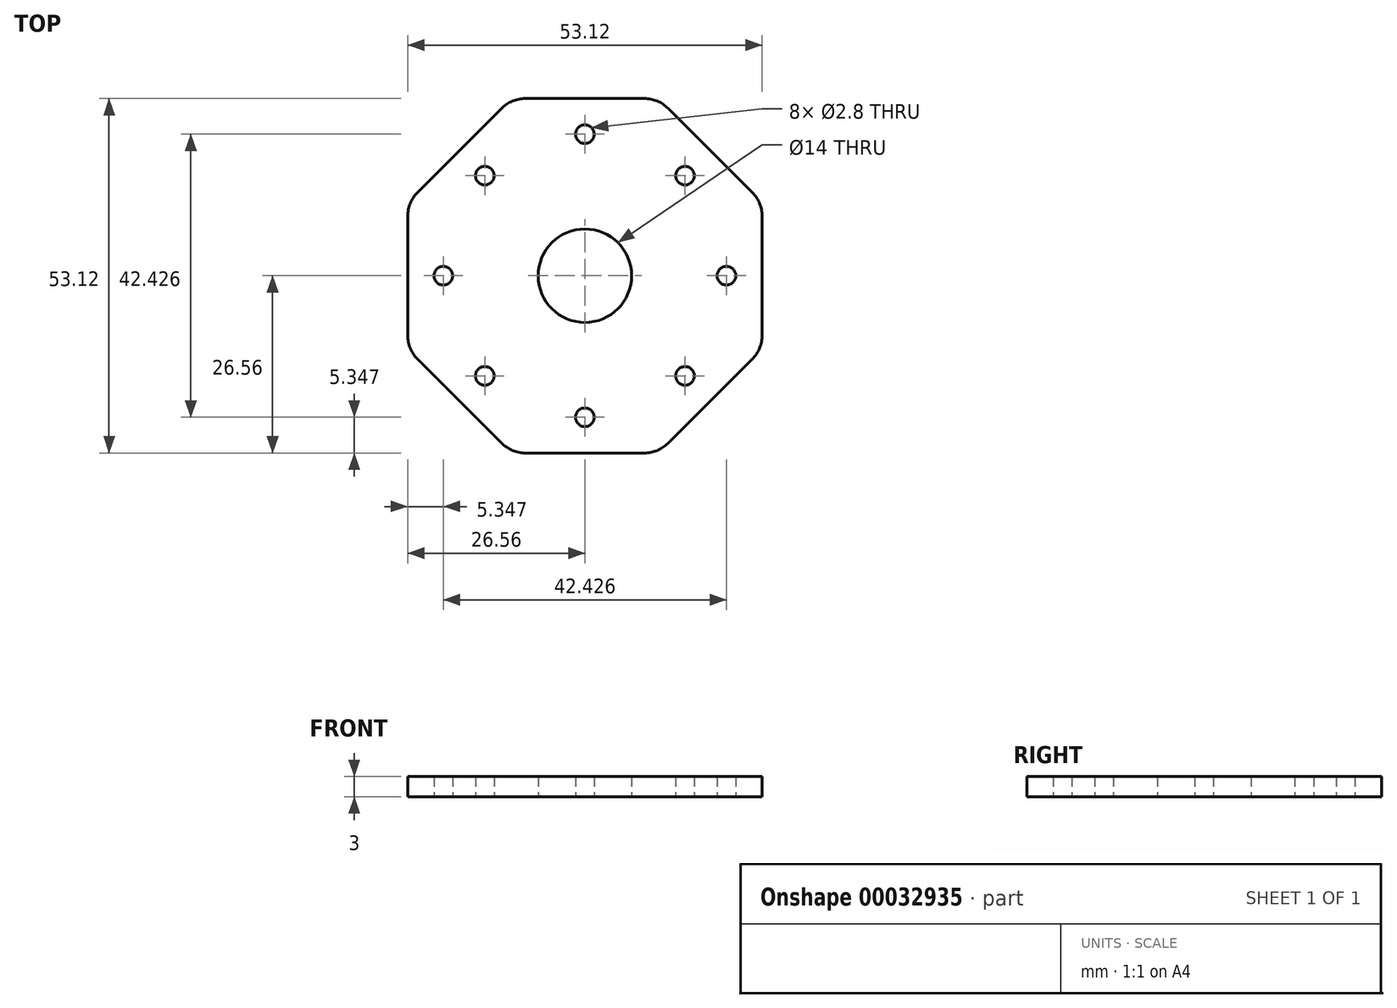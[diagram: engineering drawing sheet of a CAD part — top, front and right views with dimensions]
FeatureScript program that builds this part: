
annotation { "Feature Type Name" : "Feature", "Feature Type Description" : "" }
export const myFeature = defineFeature(function(context is Context, id is Id, definition is map)
    precondition{}
    {
        {
            var Q0;
            Q0=qCreatedBy(makeId("Top.planeOp"),FACE);
            var sketch = newSketch(context, id + "F0", { "sketchPlane" : qUnion([Q0])});
            skLineSegment(sketch, "E0.rect.bottom", {"start": v(15, -15) * mm, "end": v(-15, -15) * mm, "construction": true});
            skLineSegment(sketch, "E0.rect.top", {"start": v(15, 15) * mm, "end": v(-15, 15) * mm, "construction": true});
            skLineSegment(sketch, "E0.rect.left", {"start": v(15, -15) * mm, "end": v(15, 15) * mm, "construction": true});
            skLineSegment(sketch, "E0.rect.right", {"start": v(-15, -15) * mm, "end": v(-15, 15) * mm, "construction": true});
            skPoint(sketch, "E0.rect.middle", {"position": v(0, 0) * mm});
            skCircle(sketch, "E1.cCircle", {"center": v(0, 0) * mm, "radius": 21.21 * mm, "construction": true});
            skLineSegment(sketch, "E1.0", {"start": v(21.21, 0) * mm, "end": v(0, -21.21) * mm, "construction": true});
            skLineSegment(sketch, "E1.1", {"start": v(0, -21.21) * mm, "end": v(-21.21, 0) * mm, "construction": true});
            skLineSegment(sketch, "E1.2", {"start": v(-21.21, 0) * mm, "end": v(0, 21.21) * mm, "construction": true});
            skLineSegment(sketch, "E1.3", {"start": v(0, 21.21) * mm, "end": v(21.21, 0) * mm, "construction": true});
            skCircle(sketch, "E2", {"center": v(0, 21.21) * mm, "radius": 1.4 * mm});
            skCircle(sketch, "E3.1.0", {"center": v(-15, 15) * mm, "radius": 1.4 * mm});
            skCircle(sketch, "E3.2.0", {"center": v(-21.21, 0) * mm, "radius": 1.4 * mm});
            skCircle(sketch, "E3.3.0", {"center": v(-15, -15) * mm, "radius": 1.4 * mm});
            skCircle(sketch, "E3.4.0", {"center": v(0, -21.21) * mm, "radius": 1.4 * mm});
            skCircle(sketch, "E3.5.0", {"center": v(15, -15) * mm, "radius": 1.4 * mm});
            skCircle(sketch, "E3.6.0", {"center": v(21.21, 0) * mm, "radius": 1.4 * mm});
            skCircle(sketch, "E3.7.0", {"center": v(15, 15) * mm, "radius": 1.4 * mm});
            skCircle(sketch, "E4.cCircle", {"center": v(0, 0) * mm, "radius": 26.56 * mm, "construction": true});
            skLineSegment(sketch, "E4.0", {"start": v(-8.93, 26.56) * mm, "end": v(8.93, 26.56) * mm});
            skLineSegment(sketch, "E4.1", {"start": v(12.46, 25.1) * mm, "end": v(25.1, 12.46) * mm});
            skLineSegment(sketch, "E4.2", {"start": v(26.56, 8.93) * mm, "end": v(26.56, -8.93) * mm});
            skLineSegment(sketch, "E4.3", {"start": v(25.1, -12.46) * mm, "end": v(12.46, -25.1) * mm});
            skLineSegment(sketch, "E4.4", {"start": v(8.93, -26.56) * mm, "end": v(-8.93, -26.56) * mm});
            skLineSegment(sketch, "E4.5", {"start": v(-12.46, -25.1) * mm, "end": v(-25.1, -12.46) * mm});
            skLineSegment(sketch, "E4.6", {"start": v(-26.56, -8.93) * mm, "end": v(-26.56, 8.93) * mm});
            skLineSegment(sketch, "E4.7", {"start": v(-25.1, 12.46) * mm, "end": v(-12.46, 25.1) * mm});
            skPoint(sketch, "E4.0.midPoint", {"position": v(0, 26.56) * mm});
            skCircle(sketch, "E5", {"center": v(0, 0) * mm, "radius": 7 * mm});
            skPoint(sketch, "E6.visualSharp", {"position": v(-11, 26.56) * mm});
            skArc(sketch, "E6.filletArc", {"start": v(-8.93, 26.56) * mm, "mid": v(-10.84, 26.18) * mm, "end": v(-12.46, 25.1) * mm});
            skPoint(sketch, "E7.visualSharp", {"position": v(-26.56, 11) * mm});
            skArc(sketch, "E7.filletArc", {"start": v(-25.1, 12.46) * mm, "mid": v(-26.18, 10.84) * mm, "end": v(-26.56, 8.93) * mm});
            skPoint(sketch, "E8.visualSharp", {"position": v(-26.56, -11) * mm});
            skArc(sketch, "E8.filletArc", {"start": v(-26.56, -8.93) * mm, "mid": v(-26.18, -10.84) * mm, "end": v(-25.1, -12.46) * mm});
            skPoint(sketch, "E9.visualSharp", {"position": v(-11, -26.56) * mm});
            skArc(sketch, "E9.filletArc", {"start": v(-12.46, -25.1) * mm, "mid": v(-10.84, -26.18) * mm, "end": v(-8.93, -26.56) * mm});
            skPoint(sketch, "E10.visualSharp", {"position": v(11, -26.56) * mm});
            skArc(sketch, "E10.filletArc", {"start": v(8.93, -26.56) * mm, "mid": v(10.84, -26.18) * mm, "end": v(12.46, -25.1) * mm});
            skPoint(sketch, "E11.visualSharp", {"position": v(26.56, -11) * mm});
            skArc(sketch, "E11.filletArc", {"start": v(25.1, -12.46) * mm, "mid": v(26.18, -10.84) * mm, "end": v(26.56, -8.93) * mm});
            skPoint(sketch, "E12.visualSharp", {"position": v(26.56, 11) * mm});
            skArc(sketch, "E12.filletArc", {"start": v(26.56, 8.93) * mm, "mid": v(26.18, 10.84) * mm, "end": v(25.1, 12.46) * mm});
            skPoint(sketch, "E13.visualSharp", {"position": v(11, 26.56) * mm});
            skArc(sketch, "E13.filletArc", {"start": v(12.46, 25.1) * mm, "mid": v(10.84, 26.18) * mm, "end": v(8.93, 26.56) * mm});
            skSolve(sketch);
        }
        {
            var Q0;
            Q0=makeQuery(id+"F0.imprint","IMPRINT",FACE,{"disambiguationData":[TD([[makeQuery(id+"F0.imprint","IMPRINT",EDGE,{"derivedFrom":sQuery(id+"F0.wireOp",EDGE,"E2")}),-1.0]])]});
            extrude(context, id + "F1", {"entities" : qUnion([Q0]), "depth" : 3 * mm});
        }
    });
